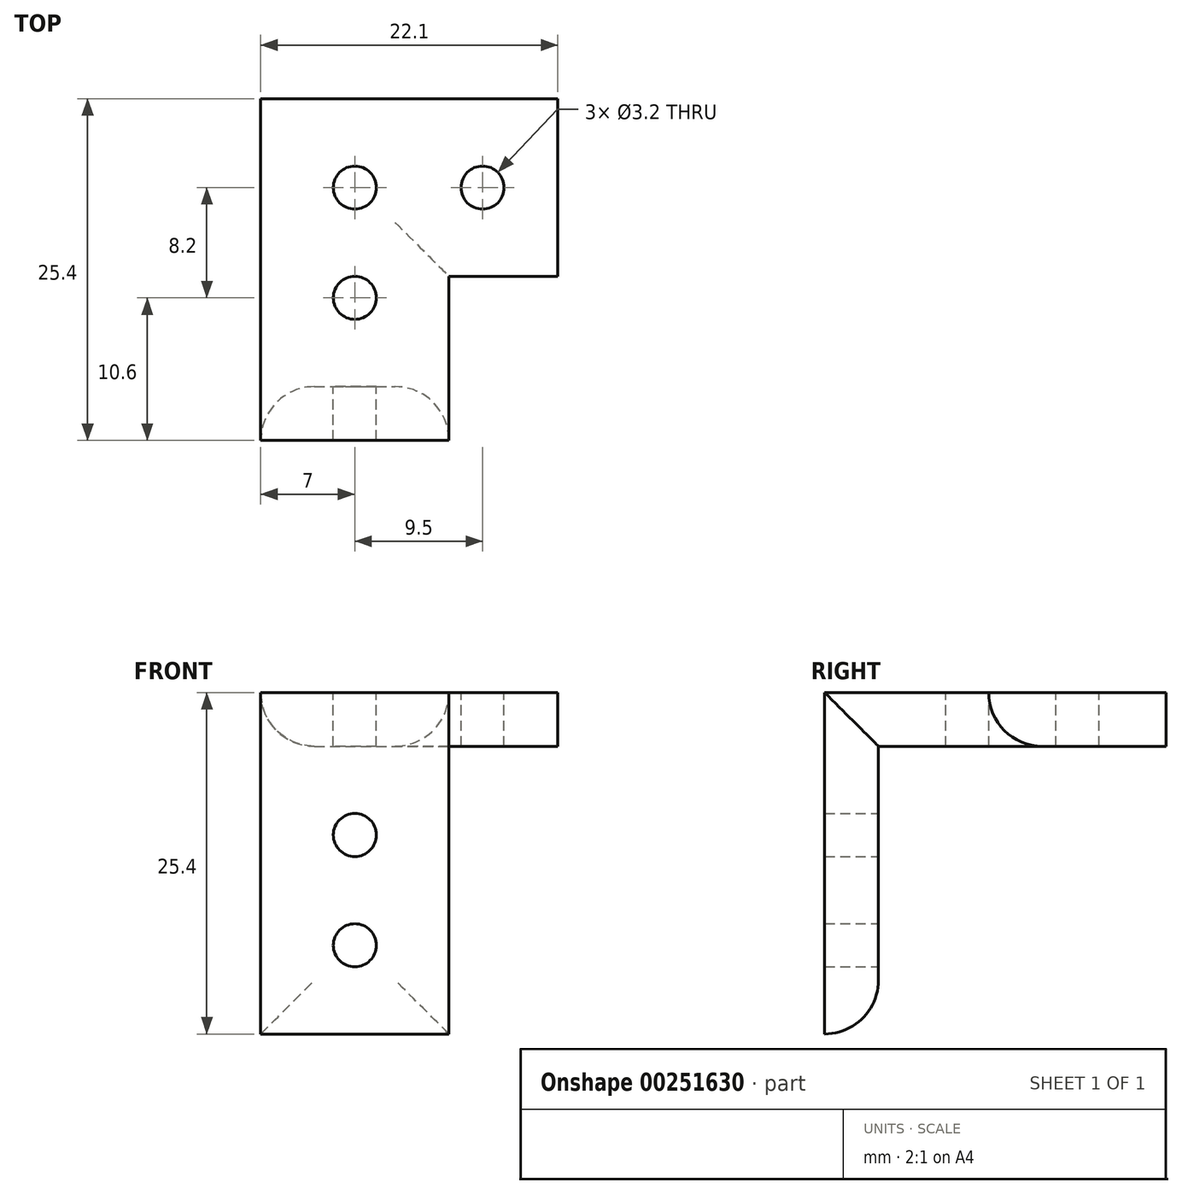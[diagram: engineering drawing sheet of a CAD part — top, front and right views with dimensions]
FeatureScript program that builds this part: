
annotation { "Feature Type Name" : "Feature", "Feature Type Description" : "" }
export const myFeature = defineFeature(function(context is Context, id is Id, definition is map)
    precondition{}
    {
        {
            var Q0;
            Q0=qCreatedBy(makeId("Top.planeOp"),FACE);
            var sketch = newSketch(context, id + "F0", { "sketchPlane" : qUnion([Q0])});
            skLineSegment(sketch, "E0", {"start": v(-7, 12.7) * mm, "end": v(-7, -12.7) * mm});
            skLineSegment(sketch, "E1", {"start": v(-7, -12.7) * mm, "end": v(7, -12.7) * mm});
            skLineSegment(sketch, "E2", {"start": v(7, -12.7) * mm, "end": v(7, -0.5) * mm});
            skLineSegment(sketch, "E3", {"start": v(7, 12.7) * mm, "end": v(-7, 12.7) * mm});
            skLineSegment(sketch, "E4", {"start": v(0, 12.7) * mm, "end": v(0, -12.7) * mm, "construction": true});
            skPoint(sketch, "E5", {"position": v(0, 0) * mm});
            skCircle(sketch, "E6", {"center": v(0, -2.1) * mm, "radius": 1.6 * mm});
            skCircle(sketch, "E7", {"center": v(0, 6.1) * mm, "radius": 1.6 * mm});
            skCircle(sketch, "E8", {"center": v(9.5, 6.1) * mm, "radius": 1.6 * mm});
            skLineSegment(sketch, "E9", {"start": v(7, 12.7) * mm, "end": v(15.1, 12.7) * mm});
            skLineSegment(sketch, "E10", {"start": v(15.1, 12.7) * mm, "end": v(15.1, -0.5) * mm});
            skLineSegment(sketch, "E11", {"start": v(15.1, -0.5) * mm, "end": v(7, -0.5) * mm});
            skLineSegment(sketch, "E12", {"start": v(7, -0.5) * mm, "end": v(7, 12.7) * mm, "construction": true});
            skLineSegment(sketch, "E13", {"start": v(-7, -8.7) * mm, "end": v(7, -8.7) * mm});
            skSolve(sketch);
        }
        {
            var Q0;
            {var subQ3=sQuery(id+"F0.wireOp",EDGE,"E3");Q0=makeQuery(id+"F0.imprint","IMPRINT",FACE,{"disambiguationData":[TD([[makeQuery(id+"F0.imprint","IMPRINT",EDGE,{"derivedFrom":subQ3}),1.0]])]});}
            extrude(context, id + "F1", {"entities" : qUnion([Q0]), "oppositeDirection" : true, "depth" : 4 * mm, "offsetDistance" : 25 * mm});
        }
        {
            var Q0;
            {var subQ0=sQuery(id+"F0.wireOp",EDGE,"E1");Q0=makeQuery(id+"F0.imprint","IMPRINT",FACE,{"disambiguationData":[TD([[makeQuery(id+"F0.imprint","IMPRINT",EDGE,{"derivedFrom":subQ0}),1.0]])]});}
            extrude(context, id + "F2", {"entities" : qUnion([Q0]), "operationType" : NewBodyOperationType.ADD, "oppositeDirection" : true, "depth" : 25.4 * mm, "offsetDistance" : 25 * mm});
        }
        {
            var Q0;
            Q0=makeQuery(id+"F2.opExtrude","SWEPT_FACE",FACE,{"disambiguationData":[OSD([sQuery(id+"F0.wireOp",EDGE,"E13")])]});
            var sketch = newSketch(context, id + "F3", { "sketchPlane" : qUnion([Q0])});
            skLineSegment(sketch, "E14", {"start": v(0, -25.4) * mm, "end": v(0, -4) * mm, "construction": true});
            skCircle(sketch, "E15", {"center": v(0, -18.8) * mm, "radius": 1.6 * mm});
            skCircle(sketch, "E16", {"center": v(0, -10.6) * mm, "radius": 1.6 * mm});
            skSolve(sketch);
        }
        {
            var Q0;
            Q0=makeQuery(id+"F3.imprint","IMPRINT",FACE,{"disambiguationData":[TD([[makeQuery(id+"F3.imprint","IMPRINT",EDGE,{"derivedFrom":sQuery(id+"F3.wireOp",EDGE,"E16")}),1.0]])]});
            var Q1;
            Q1=makeQuery(id+"F3.imprint","IMPRINT",FACE,{"disambiguationData":[TD([[makeQuery(id+"F3.imprint","IMPRINT",EDGE,{"derivedFrom":sQuery(id+"F3.wireOp",EDGE,"E15")}),1.0]])]});
            var Q2;
            Q2=makeQuery(id+"F2.opExtrude","SWEPT_FACE",FACE,{"disambiguationData":[OSD([sQuery(id+"F0.wireOp",EDGE,"E1")])]});
            extrude(context, id + "F4", {"entities" : qUnion([Q0, Q1]), "operationType" : NewBodyOperationType.REMOVE, "endBound" : BoundingType.UP_TO_SURFACE, "oppositeDirection" : true, "depth" : 25 * mm, "endBoundEntityFace" : qUnion([Q2]), "offsetDistance" : 25 * mm});
        }
        {
            var Q0;
            Q0=makeQuery(id+"F2.opExtrude","SWEPT_EDGE",EDGE,{"disambiguationData":[OSD([sQuery(id+"F0.wireOp",EDGE,"E0"),sQuery(id+"F0.wireOp",EDGE,"E13")])]});
            var Q1;
            Q1=makeQuery(id+"F2.opExtrude","CAP_EDGE",EDGE,{"disambiguationData":[OSD([sQuery(id+"F0.wireOp",EDGE,"E13")])],"isStart":false});
            var Q2;
            Q2=makeQuery(id+"F2.opExtrude","SWEPT_EDGE",EDGE,{"disambiguationData":[OSD([sQuery(id+"F0.wireOp",EDGE,"E2"),sQuery(id+"F0.wireOp",EDGE,"E13")])]});
            var Q3;
            Q3=makeQuery(id+"F1.opExtrude","CAP_EDGE",EDGE,{"disambiguationData":[OSD([sQuery(id+"F0.wireOp",EDGE,"E0")])],"isStart":false});
            var Q4;
            Q4=makeQuery(id+"F1.opExtrude","CAP_EDGE",EDGE,{"disambiguationData":[OSD([sQuery(id+"F0.wireOp",EDGE,"E2")])],"isStart":false});
            var Q5;
            Q5=makeQuery(id+"F1.opExtrude","CAP_EDGE",EDGE,{"disambiguationData":[OSD([sQuery(id+"F0.wireOp",EDGE,"E11")])],"isStart":false});
            fillet(context, id + "F5", {"entities" : qUnion([Q0, Q1, Q2, Q3, Q4, Q5]), "radius" : 4 * mm, "tangentPropagation" : true, "allowEdgeOverflow" : false});
        }
    });
